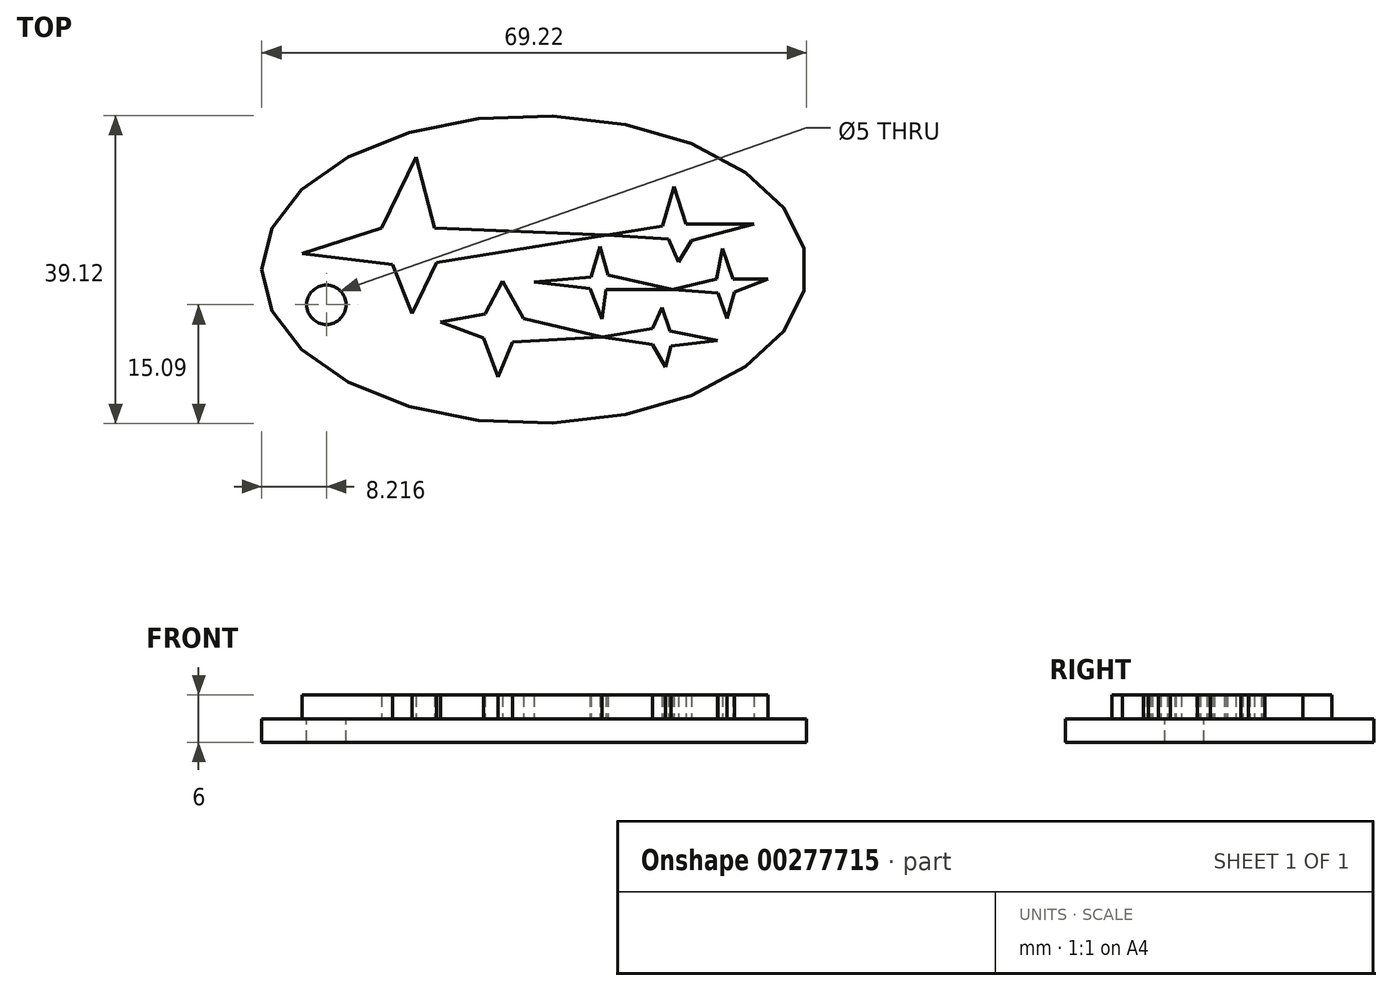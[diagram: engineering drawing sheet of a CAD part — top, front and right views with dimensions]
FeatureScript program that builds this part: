
annotation { "Feature Type Name" : "Feature", "Feature Type Description" : "" }
export const myFeature = defineFeature(function(context is Context, id is Id, definition is map)
    precondition{}
    {
        {
            var Q0;
            Q0=qCreatedBy(makeId("Top.planeOp"),FACE);
            var sketch = newSketch(context, id + "F0", { "sketchPlane" : qUnion([Q0])});
            skEllipse(sketch, "E0", {"center": v(0, 0) * mm, "majorRadius": 19.56 * mm, "minorRadius": 34.6 * mm, "majorAxis": v(0, 1)});
            skSolve(sketch);
        }
        {
            var Q0;
            Q0=qSketchRegion(id+"F0",true);
            extrude(context, id + "F1", {"entities" : qUnion([Q0]), "depth" : 3 * mm});
        }
        {
            var Q0;
            Q0=makeQuery(id+"F1.opExtrude","CAP_FACE",FACE,{"disambiguationData":[OSD([sQuery(id+"F0.wireOp",EDGE,"E0")])],"isStart":false});
            var sketch = newSketch(context, id + "F2", { "sketchPlane" : qUnion([Q0])});
            skLineSegment(sketch, "E1", {"start": v(-19.4, 5.3) * mm, "end": v(-14.99, 14.29) * mm});
            skLineSegment(sketch, "E2", {"start": v(-14.99, 14.29) * mm, "end": v(-12.63, 5.3) * mm});
            skLineSegment(sketch, "E3", {"start": v(-12.39, 0.87) * mm, "end": v(-15.49, -5.57) * mm});
            skLineSegment(sketch, "E4", {"start": v(-15.49, -5.57) * mm, "end": v(-17.96, 0.62) * mm});
            skLineSegment(sketch, "E5", {"start": v(-12.63, 5.3) * mm, "end": v(9.26, 4.39) * mm});
            skLineSegment(sketch, "E6", {"start": v(9.26, 4.39) * mm, "end": v(-12.39, 0.87) * mm});
            skLineSegment(sketch, "E7", {"start": v(-17.96, 0.62) * mm, "end": v(-29.48, 2.03) * mm});
            skLineSegment(sketch, "E8", {"start": v(-29.48, 2.03) * mm, "end": v(-19.4, 5.3) * mm});
            skLineSegment(sketch, "E9", {"start": v(9.26, 4.39) * mm, "end": v(16.33, 5.53) * mm});
            skLineSegment(sketch, "E10", {"start": v(16.33, 5.53) * mm, "end": v(17.73, 10.55) * mm});
            skLineSegment(sketch, "E11", {"start": v(17.73, 10.55) * mm, "end": v(19.3, 5.75) * mm});
            skLineSegment(sketch, "E12", {"start": v(19.3, 5.75) * mm, "end": v(27.9, 5.75) * mm});
            skLineSegment(sketch, "E13", {"start": v(27.9, 5.75) * mm, "end": v(19.96, 3.69) * mm});
            skLineSegment(sketch, "E14", {"start": v(19.96, 3.69) * mm, "end": v(18.3, 0.96) * mm});
            skLineSegment(sketch, "E15", {"start": v(18.3, 0.96) * mm, "end": v(17.07, 3.85) * mm});
            skLineSegment(sketch, "E16", {"start": v(17.07, 3.85) * mm, "end": v(9.26, 4.39) * mm});
            skLineSegment(sketch, "E17", {"start": v(8.39, 2.94) * mm, "end": v(7.23, -0.94) * mm});
            skLineSegment(sketch, "E18", {"start": v(7.23, -0.94) * mm, "end": v(0, -1.6) * mm});
            skLineSegment(sketch, "E19", {"start": v(0, -1.6) * mm, "end": v(7.06, -2.43) * mm});
            skLineSegment(sketch, "E20", {"start": v(7.06, -2.43) * mm, "end": v(8.64, -6.32) * mm});
            skLineSegment(sketch, "E21", {"start": v(8.64, -6.32) * mm, "end": v(9.13, -2.51) * mm});
            skLineSegment(sketch, "E22", {"start": v(9.13, -2.51) * mm, "end": v(17.56, -2.51) * mm});
            skLineSegment(sketch, "E23", {"start": v(17.56, -2.51) * mm, "end": v(9.38, -0.7) * mm});
            skLineSegment(sketch, "E24", {"start": v(9.38, -0.7) * mm, "end": v(8.39, 2.94) * mm});
            skLineSegment(sketch, "E25", {"start": v(17.56, -2.51) * mm, "end": v(23.19, -1.2) * mm});
            skLineSegment(sketch, "E26", {"start": v(23.19, -1.2) * mm, "end": v(23.93, 2.7) * mm});
            skLineSegment(sketch, "E27", {"start": v(23.93, 2.7) * mm, "end": v(25.25, -1.2) * mm});
            skLineSegment(sketch, "E28", {"start": v(25.25, -1.2) * mm, "end": v(29.72, -1.2) * mm});
            skLineSegment(sketch, "E29", {"start": v(29.72, -1.2) * mm, "end": v(25.42, -2.84) * mm});
            skLineSegment(sketch, "E30", {"start": v(25.42, -2.84) * mm, "end": v(24.5, -6.23) * mm});
            skLineSegment(sketch, "E31", {"start": v(24.5, -6.23) * mm, "end": v(23.35, -3) * mm});
            skLineSegment(sketch, "E32", {"start": v(23.35, -3) * mm, "end": v(17.56, -2.51) * mm});
            skLineSegment(sketch, "E33", {"start": v(16.24, -4.83) * mm, "end": v(15, -7.47) * mm});
            skLineSegment(sketch, "E34", {"start": v(15, -7.47) * mm, "end": v(8.64, -8.55) * mm});
            skLineSegment(sketch, "E35", {"start": v(8.64, -8.55) * mm, "end": v(15, -9.54) * mm});
            skLineSegment(sketch, "E36", {"start": v(15, -9.54) * mm, "end": v(16.65, -12.35) * mm});
            skLineSegment(sketch, "E37", {"start": v(16.65, -12.35) * mm, "end": v(17.4, -9.7) * mm});
            skLineSegment(sketch, "E38", {"start": v(17.4, -9.7) * mm, "end": v(23.27, -9.04) * mm});
            skLineSegment(sketch, "E39", {"start": v(23.27, -9.04) * mm, "end": v(17.23, -7.8) * mm});
            skLineSegment(sketch, "E40", {"start": v(17.23, -7.8) * mm, "end": v(16.24, -4.83) * mm});
            skLineSegment(sketch, "E41", {"start": v(8.64, -8.55) * mm, "end": v(-1.37, -6.23) * mm});
            skLineSegment(sketch, "E42", {"start": v(-1.37, -6.23) * mm, "end": v(-4.01, -1.44) * mm});
            skLineSegment(sketch, "E43", {"start": v(-4.01, -1.44) * mm, "end": v(-6.25, -5.66) * mm});
            skLineSegment(sketch, "E44", {"start": v(-6.25, -5.66) * mm, "end": v(-11.87, -6.65) * mm});
            skLineSegment(sketch, "E45", {"start": v(-11.87, -6.65) * mm, "end": v(-6.41, -8.71) * mm});
            skLineSegment(sketch, "E46", {"start": v(-6.41, -8.71) * mm, "end": v(-4.6, -13.67) * mm});
            skLineSegment(sketch, "E47", {"start": v(-4.6, -13.67) * mm, "end": v(-2.77, -9.21) * mm});
            skLineSegment(sketch, "E48", {"start": v(-2.77, -9.21) * mm, "end": v(8.64, -8.55) * mm});
            skSolve(sketch);
        }
        {
            var Q0;
            Q0=qSketchRegion(id+"F2",true);
            extrude(context, id + "F3", {"entities" : qUnion([Q0]), "depth" : 3 * mm});
        }
        {
            var Q0;
            Q0=makeQuery(id+"F1.opExtrude","CAP_FACE",FACE,{"disambiguationData":[OSD([sQuery(id+"F0.wireOp",EDGE,"E0")])],"isStart":false});
            var sketch = newSketch(context, id + "F4", { "sketchPlane" : qUnion([Q0])});
            skCircle(sketch, "E49", {"center": v(-26.4, -4.47) * mm, "radius": 2.5 * mm});
            skSolve(sketch);
        }
        {
            var Q0;
            Q0=qSketchRegion(id+"F4",true);
            extrude(context, id + "F5", {"entities" : qUnion([Q0]), "operationType" : NewBodyOperationType.REMOVE, "endBound" : BoundingType.THROUGH_ALL, "oppositeDirection" : true, "depth" : 25 * mm});
        }
    });
